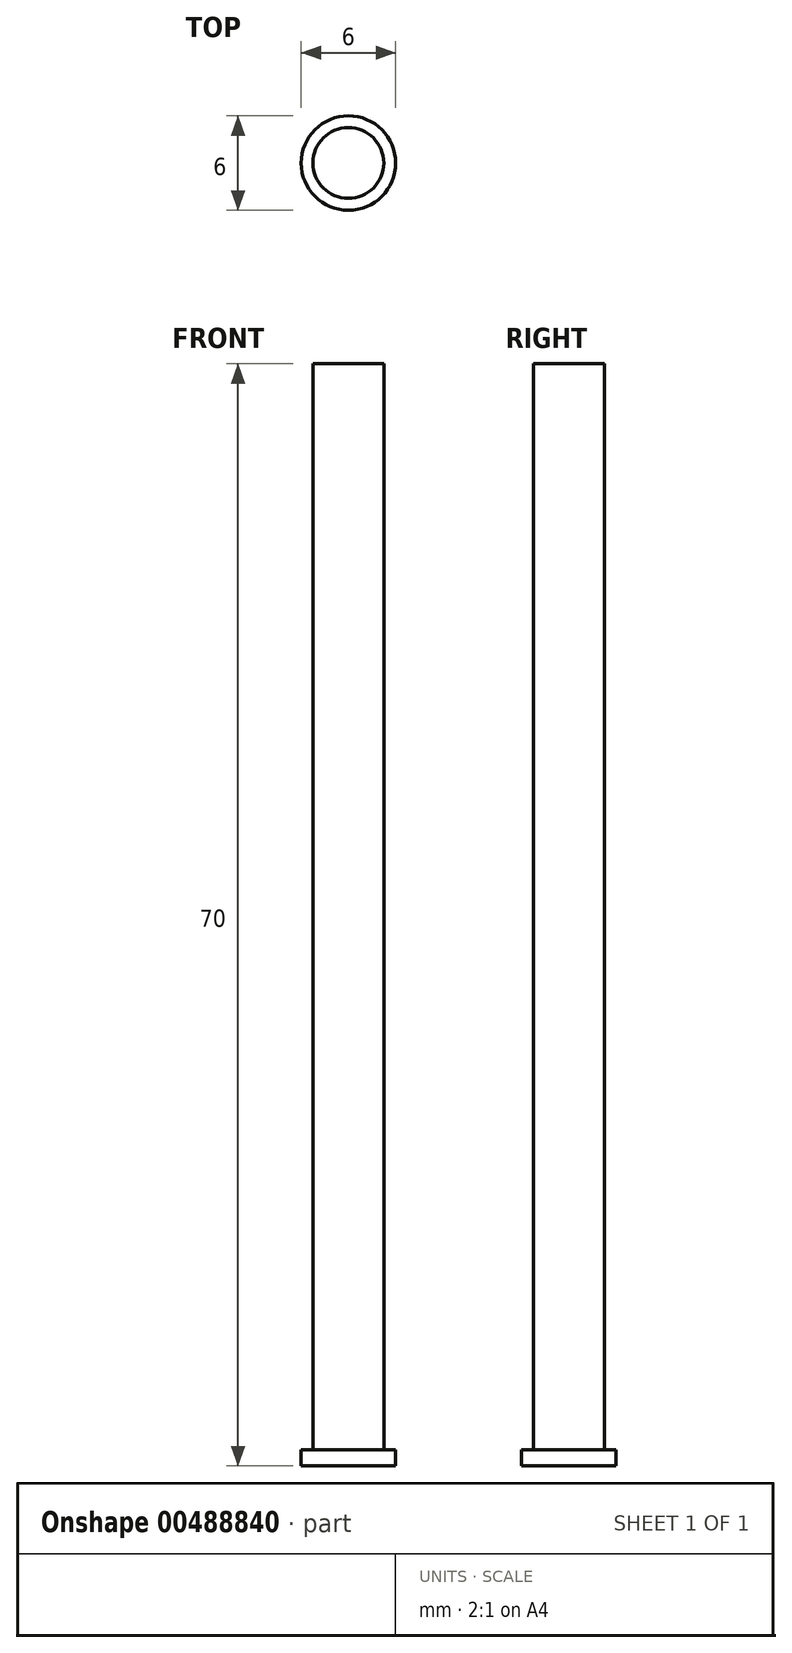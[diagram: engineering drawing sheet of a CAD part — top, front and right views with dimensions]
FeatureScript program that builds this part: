
annotation { "Feature Type Name" : "Feature", "Feature Type Description" : "" }
export const myFeature = defineFeature(function(context is Context, id is Id, definition is map)
    precondition{}
    {
        {
            var Q0;
            Q0=qCreatedBy(makeId("Top.planeOp"),FACE);
            var sketch = newSketch(context, id + "F0", { "sketchPlane" : qUnion([Q0])});
            skCircle(sketch, "E0", {"center": v(0, 0) * mm, "radius": 2.25 * mm});
            skSolve(sketch);
        }
        {
            var Q0;
            Q0=makeQuery(id+"F0.imprint","IMPRINT",FACE,{"disambiguationData":[TD([[makeQuery(id+"F0.imprint","IMPRINT",EDGE,{"derivedFrom":sQuery(id+"F0.wireOp",EDGE,"E0")}),1.0]])]});
            extrude(context, id + "F1", {"entities" : qUnion([Q0]), "depth" : 70 * mm});
        }
        {
            var Q0;
            Q0=qCreatedBy(makeId("Top.planeOp"),FACE);
            var sketch = newSketch(context, id + "F2", { "sketchPlane" : qUnion([Q0])});
            skCircle(sketch, "E1", {"center": v(0, 0) * mm, "radius": 3 * mm});
            skCircle(sketch, "E2", {"center": v(0, 0) * mm, "radius": 2.25 * mm});
            skSolve(sketch);
        }
        {
            var Q0;
            Q0=makeQuery(id+"F2.imprint","IMPRINT",FACE,{"disambiguationData":[TD([[makeQuery(id+"F2.imprint","IMPRINT",EDGE,{"derivedFrom":sQuery(id+"F2.wireOp",EDGE,"E1")}),1.0]])]});
            extrude(context, id + "F3", {"entities" : qUnion([Q0]), "operationType" : NewBodyOperationType.ADD, "depth" : 1 * mm});
        }
    });
